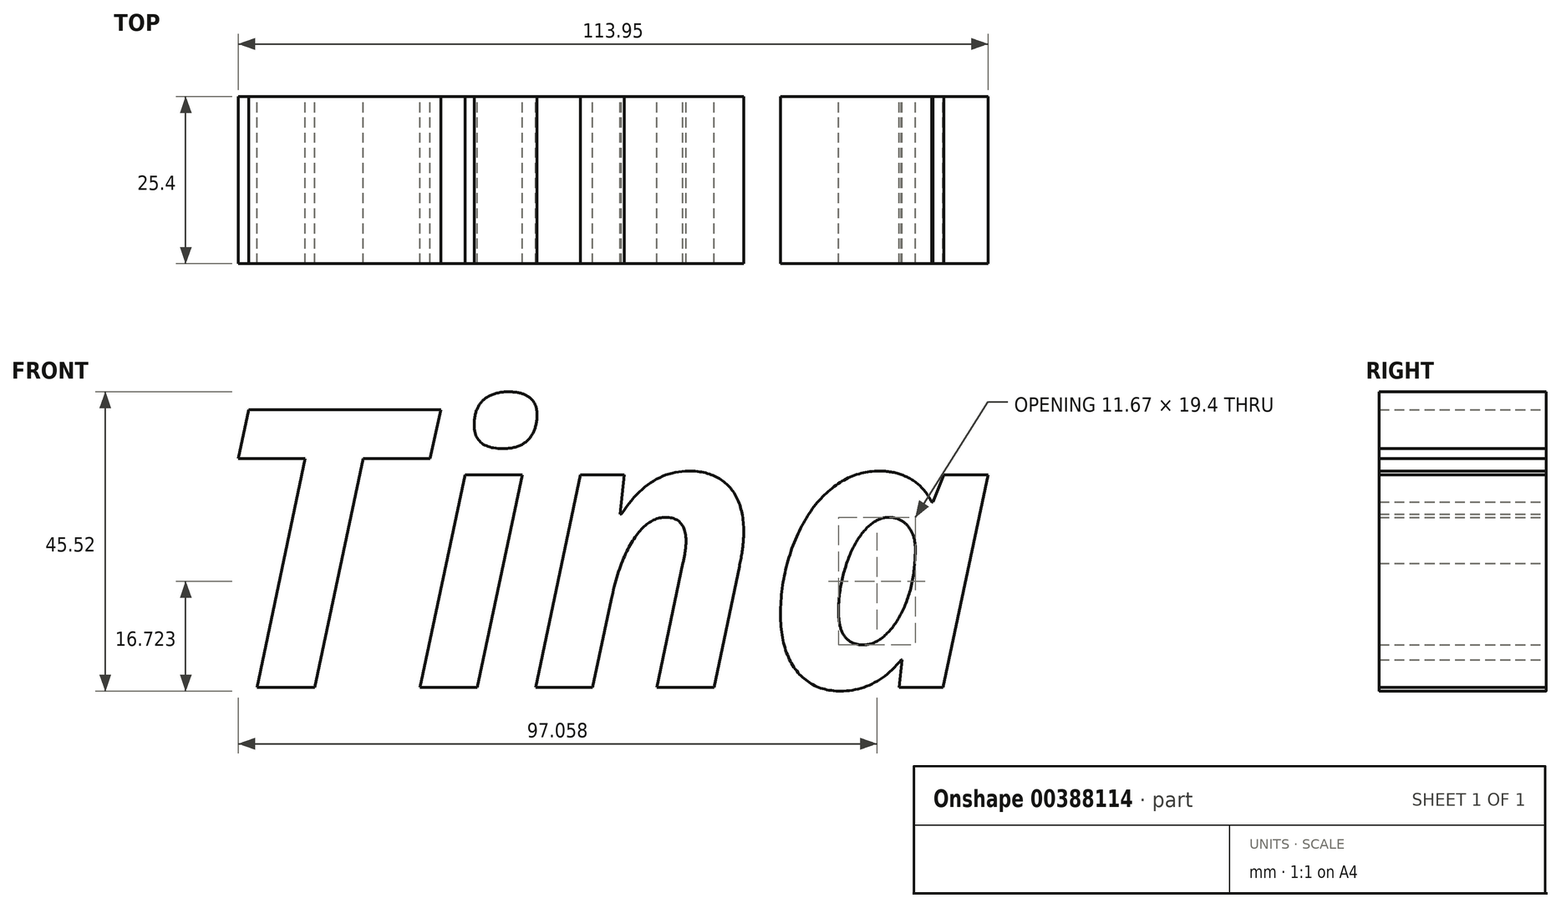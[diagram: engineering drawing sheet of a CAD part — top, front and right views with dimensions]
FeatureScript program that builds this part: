
annotation { "Feature Type Name" : "Feature", "Feature Type Description" : "" }
export const myFeature = defineFeature(function(context is Context, id is Id, definition is map)
    precondition{}
    {
        {
            var Q0;
            Q0=qCreatedBy(makeId("Front.planeOp"),FACE);
            var sketch = newSketch(context, id + "F0", { "sketchPlane" : qUnion([Q0])});
            skText(sketch, "E0", { "text": "Tina", "fontName": "OpenSans-BoldItalic.ttf"});
            const initialGuessF0  = {"E0": [-0.06563, -0.02724, 1, 0, 0.04258]};
            skSetInitialGuess(sketch, initialGuessF0);
            skSolve(sketch);
        }
        {
            var Q0;
            Q0=makeQuery(id+"F0.imprint","IMPRINT",FACE,{"disambiguationData":[TD([[makeQuery(id+"F0.imprint","IMPRINT",EDGE,{"derivedFrom":sQuery(id+"F0.wireOp",EDGE,"E0.sketch_text.stroke-0")}),-1.0]])]});
            var Q1;
            Q1 = qSketchRegion(id + "F0", true);
            extrude(context, id + "F1", {"entities" : qUnion([Q0, Q1]), "depth" : 25.4 * mm});
        }
    });
